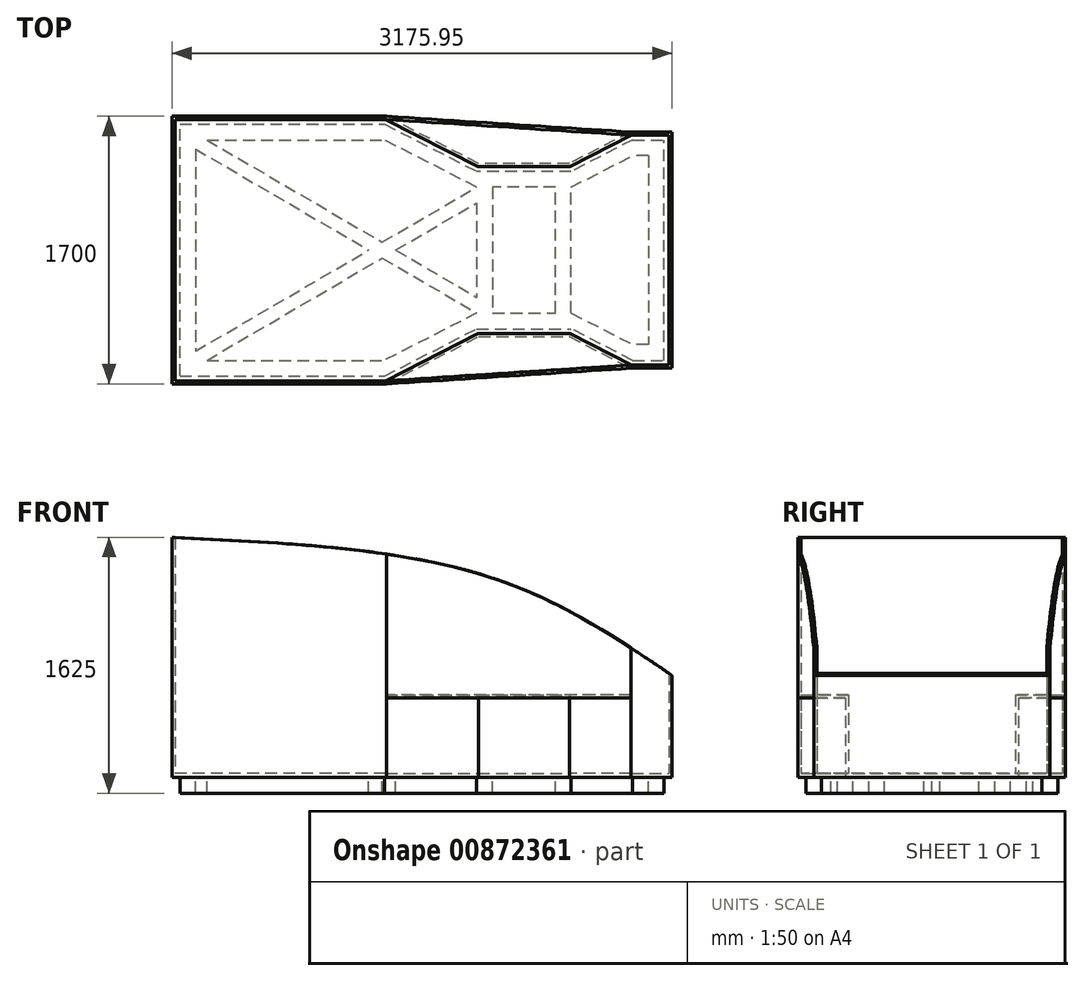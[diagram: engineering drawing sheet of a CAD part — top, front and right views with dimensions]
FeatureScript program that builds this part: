
annotation { "Feature Type Name" : "Feature", "Feature Type Description" : "" }
export const myFeature = defineFeature(function(context is Context, id is Id, definition is map)
    precondition{}
    {
        {
            var Q0;
            Q0=qCreatedBy(makeId("Top.planeOp"),FACE);
            var sketch = newSketch(context, id + "F0", { "sketchPlane" : qUnion([Q0])});
            skLineSegment(sketch, "E0", {"start": v(2008.61, 739.14) * mm, "end": v(1908.61, 739.14) * mm});
            skLineSegment(sketch, "E1.MirrorCS", {"start": v(-476.96, 1439.14) * mm, "end": v(-476.96, 1539.14) * mm});
            skLineSegment(sketch, "E2.MirrorCS", {"start": v(1408.61, 1039.14) * mm, "end": v(1408.61, 739.14) * mm});
            skLineSegment(sketch, "E3.MirrorCS", {"start": v(-476.96, 1539.14) * mm, "end": v(823.04, 1539.14) * mm});
            skLineSegment(sketch, "E4.MirrorCS", {"start": v(823.04, 1539.14) * mm, "end": v(1408.61, 1239.14) * mm});
            skLineSegment(sketch, "E5.MirrorCS", {"start": v(1408.61, 1139.14) * mm, "end": v(823.04, 1439.14) * mm});
            skLineSegment(sketch, "E6.MirrorCS", {"start": v(-305.54, 1439.14) * mm, "end": v(823.04, 1439.14) * mm});
            skLineSegment(sketch, "E7.MirrorCS", {"start": v(1408.61, 1239.14) * mm, "end": v(1708.61, 1239.14) * mm});
            skLineSegment(sketch, "E8.MirrorCS", {"start": v(1508.61, 739.14) * mm, "end": v(1508.61, 1139.14) * mm});
            skLineSegment(sketch, "E9.MirrorCS", {"start": v(1708.61, 1139.14) * mm, "end": v(1508.61, 1139.14) * mm});
            skLineSegment(sketch, "E10.MirrorCS", {"start": v(1708.61, 1139.14) * mm, "end": v(1908.61, 1139.14) * mm});
            skLineSegment(sketch, "E11.MirrorCS", {"start": v(1908.61, 739.14) * mm, "end": v(1908.61, 1139.14) * mm});
            skLineSegment(sketch, "E12.MirrorCS", {"start": v(2399, 1439.14) * mm, "end": v(2008.61, 1239.14) * mm});
            skLineSegment(sketch, "E13.MirrorCS", {"start": v(2008.61, 1139.14) * mm, "end": v(2399, 1339.14) * mm});
            skLineSegment(sketch, "E14.MirrorCS", {"start": v(2008.61, 1239.14) * mm, "end": v(1708.61, 1239.14) * mm});
            skLineSegment(sketch, "E15.MirrorCS", {"start": v(2008.61, 1139.14) * mm, "end": v(2008.61, 739.14) * mm});
            skLineSegment(sketch, "E16", {"start": v(2399, 1439.14) * mm, "end": v(2599, 1439.14) * mm});
            skLineSegment(sketch, "E17", {"start": v(2599, 1439.14) * mm, "end": v(2599, 1339.14) * mm});
            skLineSegment(sketch, "E18", {"start": v(2499, 1339.14) * mm, "end": v(2399, 1339.14) * mm});
            skLineSegment(sketch, "E19", {"start": v(2599, 739.14) * mm, "end": v(2599, 1339.14) * mm});
            skLineSegment(sketch, "E20", {"start": v(2499, 1339.14) * mm, "end": v(2499, 739.14) * mm});
            skLineSegment(sketch, "E21.MirrorCS", {"start": v(2599, 39.14) * mm, "end": v(2599, 139.14) * mm});
            skLineSegment(sketch, "E22.MirrorCS", {"start": v(-476.96, 39.14) * mm, "end": v(-476.96, -60.86) * mm});
            skLineSegment(sketch, "E23.MirrorCS", {"start": v(2499, 139.14) * mm, "end": v(2399, 139.14) * mm});
            skLineSegment(sketch, "E24.MirrorCS", {"start": v(2399, 39.14) * mm, "end": v(2599, 39.14) * mm});
            skLineSegment(sketch, "E25.MirrorCS", {"start": v(1408.61, 239.14) * mm, "end": v(1708.61, 239.14) * mm});
            skLineSegment(sketch, "E26.MirrorCS", {"start": v(-305.54, 39.14) * mm, "end": v(823.04, 39.14) * mm});
            skLineSegment(sketch, "E27.MirrorCS", {"start": v(-476.96, -60.86) * mm, "end": v(823.04, -60.86) * mm});
            skLineSegment(sketch, "E28.MirrorCS", {"start": v(823.04, -60.86) * mm, "end": v(1408.61, 239.14) * mm});
            skLineSegment(sketch, "E29.MirrorCS", {"start": v(1708.61, 339.14) * mm, "end": v(1908.61, 339.14) * mm});
            skLineSegment(sketch, "E30.MirrorCS", {"start": v(1408.61, 339.14) * mm, "end": v(823.04, 39.14) * mm});
            skLineSegment(sketch, "E31.MirrorCS", {"start": v(2008.61, 339.14) * mm, "end": v(2399, 139.14) * mm});
            skLineSegment(sketch, "E32.MirrorCS", {"start": v(1408.61, 439.14) * mm, "end": v(1408.61, 739.14) * mm});
            skLineSegment(sketch, "E33.MirrorCS", {"start": v(1708.61, 339.14) * mm, "end": v(1508.61, 339.14) * mm});
            skLineSegment(sketch, "E34.MirrorCS", {"start": v(2399, 39.14) * mm, "end": v(2008.61, 239.14) * mm});
            skLineSegment(sketch, "E35.MirrorCS", {"start": v(1508.61, 739.14) * mm, "end": v(1508.61, 339.14) * mm});
            skLineSegment(sketch, "E36.MirrorCS", {"start": v(1908.61, 739.14) * mm, "end": v(1908.61, 339.14) * mm});
            skLineSegment(sketch, "E37.MirrorCS", {"start": v(2599, 739.14) * mm, "end": v(2599, 139.14) * mm});
            skLineSegment(sketch, "E38.MirrorCS", {"start": v(2499, 139.14) * mm, "end": v(2499, 739.14) * mm});
            skLineSegment(sketch, "E39.MirrorCS", {"start": v(2008.61, 339.14) * mm, "end": v(2008.61, 739.14) * mm});
            skLineSegment(sketch, "E40.MirrorCS", {"start": v(2008.61, 239.14) * mm, "end": v(1708.61, 239.14) * mm});
            skPoint(sketch, "E41.MirrorCS.end.orphan", {"position": v(1018.23, 39.14) * mm});
            skPoint(sketch, "E42.end.orphan", {"position": v(1018.23, 1439.14) * mm});
            skLineSegment(sketch, "E43", {"start": v(-376.96, 1380.8) * mm, "end": v(722.95, 739.14) * mm});
            skLineSegment(sketch, "E44", {"start": v(-376.96, 97.48) * mm, "end": v(722.95, 739.14) * mm});
            skPoint(sketch, "E45", {"position": v(-305.54, 39.14) * mm});
            skPoint(sketch, "E46", {"position": v(1408.61, 1039.14) * mm});
            skLineSegment(sketch, "E47", {"start": v(-305.54, 39.14) * mm, "end": v(808.66, 689.14) * mm});
            skLineSegment(sketch, "E48", {"start": v(-305.54, 1439.14) * mm, "end": v(808.66, 789.14) * mm});
            skLineSegment(sketch, "E49.trimOffspring", {"start": v(808.66, 689.14) * mm, "end": v(1408.61, 339.14) * mm});
            skLineSegment(sketch, "E50.trimOffspring", {"start": v(808.66, 789.14) * mm, "end": v(1408.61, 1139.14) * mm});
            skLineSegment(sketch, "E51.trimOffspring", {"start": v(894.37, 739.14) * mm, "end": v(1408.61, 439.14) * mm});
            skLineSegment(sketch, "E52.trimOffspring", {"start": v(894.37, 739.14) * mm, "end": v(1408.61, 1039.14) * mm});
            skLineSegment(sketch, "E53", {"start": v(-476.96, 39.14) * mm, "end": v(-476.96, 1439.14) * mm});
            skLineSegment(sketch, "E54", {"start": v(-376.96, 1380.8) * mm, "end": v(-376.96, 97.48) * mm});
            skPoint(sketch, "E55", {"position": v(1608.61, 289.14) * mm});
            skPoint(sketch, "E56", {"position": v(1808.61, 289.14) * mm});
            skPoint(sketch, "E57", {"position": v(1608.61, 1189.14) * mm});
            skPoint(sketch, "E58", {"position": v(1808.61, 1189.14) * mm});
            skPoint(sketch, "E59.MirrorCS.end.orphan", {"position": v(1508.61, 739.14) * mm});
            skPoint(sketch, "E59.MirrorCS.start.orphan", {"position": v(1408.61, 739.14) * mm});
            skPoint(sketch, "E60.MirrorCS.end.orphan", {"position": v(1908.61, 739.14) * mm});
            skPoint(sketch, "E60.MirrorCS.start.orphan", {"position": v(2008.61, 739.14) * mm});
            skSolve(sketch);
        }
        {
            var Q0;
            Q0=makeQuery(id+"F0.imprint","IMPRINT",FACE,{"disambiguationData":[TD([[makeQuery(id+"F0.imprint","IMPRINT",EDGE,{"derivedFrom":sQuery(id+"F0.wireOp",EDGE,"E1.MirrorCS")}),-1.0]])]});
            extrude(context, id + "F1", {"entities" : qUnion([Q0]), "depth" : -100 * mm, "offsetDistance" : 25 * mm});
        }
        {
            var Q0;
            Q0=makeQuery(id+"F0.imprint","IMPRINT",FACE,{"disambiguationData":[TD([[makeQuery(id+"F0.imprint","IMPRINT",EDGE,{"derivedFrom":sQuery(id+"F0.wireOp",EDGE,"E1.MirrorCS")}),-1.0]])]});
            var sketch = newSketch(context, id + "F2", { "sketchPlane" : qUnion([Q0])});
            skLineSegment(sketch, "E61.0", {"start": v(1420.68, 189.14) * mm, "end": v(1708.61, 189.14) * mm});
            skLineSegment(sketch, "E61.1", {"start": v(835.1, -110.86) * mm, "end": v(1420.68, 189.14) * mm});
            skLineSegment(sketch, "E61.2", {"start": v(-526.96, -110.86) * mm, "end": v(835.1, -110.86) * mm});
            skLineSegment(sketch, "E61.3", {"start": v(-526.96, 39.14) * mm, "end": v(-526.96, -110.86) * mm});
            skLineSegment(sketch, "E61.4", {"start": v(-526.96, 1439.14) * mm, "end": v(-526.96, 39.14) * mm});
            skLineSegment(sketch, "E61.5", {"start": v(1708.61, 189.14) * mm, "end": v(1996.55, 189.14) * mm});
            skLineSegment(sketch, "E61.6", {"start": v(-526.96, 1589.14) * mm, "end": v(-526.96, 1439.14) * mm});
            skLineSegment(sketch, "E61.7", {"start": v(835.1, 1589.14) * mm, "end": v(-526.96, 1589.14) * mm});
            skLineSegment(sketch, "E61.8", {"start": v(1420.68, 1289.14) * mm, "end": v(835.1, 1589.14) * mm});
            skLineSegment(sketch, "E61.9", {"start": v(2649, 139.14) * mm, "end": v(2649, 739.14) * mm});
            skLineSegment(sketch, "E61.10", {"start": v(2649, -10.86) * mm, "end": v(2649, 139.14) * mm});
            skLineSegment(sketch, "E61.11", {"start": v(2386.93, -10.86) * mm, "end": v(2649, -10.86) * mm});
            skLineSegment(sketch, "E61.12", {"start": v(1996.55, 189.14) * mm, "end": v(2386.93, -10.86) * mm});
            skLineSegment(sketch, "E61.13", {"start": v(2649, 739.14) * mm, "end": v(2649, 1339.14) * mm});
            skLineSegment(sketch, "E61.14", {"start": v(2649, 1339.14) * mm, "end": v(2649, 1489.14) * mm});
            skLineSegment(sketch, "E61.15", {"start": v(2649, 1489.14) * mm, "end": v(2386.93, 1489.14) * mm});
            skLineSegment(sketch, "E61.16", {"start": v(2386.93, 1489.14) * mm, "end": v(1996.55, 1289.14) * mm});
            skLineSegment(sketch, "E61.17", {"start": v(1996.55, 1289.14) * mm, "end": v(1708.61, 1289.14) * mm});
            skLineSegment(sketch, "E61.18", {"start": v(1708.61, 1289.14) * mm, "end": v(1420.68, 1289.14) * mm});
            skSolve(sketch);
        }
        {
            var Q0;
            Q0=makeQuery(id+"F2.imprint","IMPRINT",FACE,{"disambiguationData":[TD([[makeQuery(id+"F2.imprint","IMPRINT",EDGE,{"derivedFrom":sQuery(id+"F2.wireOp",EDGE,"E61.0")}),1.0]])]});
            var Q1;
            Q1=makeQuery(id+"F2.imprint","IMPRINT",FACE,{"disambiguationData":[TD([[makeQuery(id+"F2.imprint","IMPRINT",EDGE,{"derivedFrom":makeQuery(id+"F0.imprint","IMPRINT",EDGE,{"derivedFrom":sQuery(id+"F0.wireOp",EDGE,"E1.MirrorCS")})}),-1.0]])]});
            var Q2;
            Q2=makeQuery(id+"F2.imprint","IMPRINT",FACE,{"disambiguationData":[TD([[makeQuery(id+"F2.imprint","IMPRINT",EDGE,{"derivedFrom":makeQuery(id+"F0.imprint","IMPRINT",EDGE,{"derivedFrom":sQuery(id+"F0.wireOp",EDGE,"E8.MirrorCS")})}),-1.0]])]});
            var Q3;
            Q3=makeQuery(id+"F2.imprint","IMPRINT",FACE,{"disambiguationData":[TD([[makeQuery(id+"F2.imprint","IMPRINT",EDGE,{"derivedFrom":makeQuery(id+"F0.imprint","IMPRINT",EDGE,{"derivedFrom":sQuery(id+"F0.wireOp",EDGE,"E2.MirrorCS")})}),-1.0]])]});
            var Q4;
            Q4=makeQuery(id+"F2.imprint","IMPRINT",FACE,{"disambiguationData":[TD([[makeQuery(id+"F2.imprint","IMPRINT",EDGE,{"derivedFrom":makeQuery(id+"F0.imprint","IMPRINT",EDGE,{"derivedFrom":sQuery(id+"F0.wireOp",EDGE,"E26.MirrorCS")})}),1.0]])]});
            var Q5;
            Q5=makeQuery(id+"F2.imprint","IMPRINT",FACE,{"disambiguationData":[TD([[makeQuery(id+"F2.imprint","IMPRINT",EDGE,{"derivedFrom":makeQuery(id+"F0.imprint","IMPRINT",EDGE,{"derivedFrom":sQuery(id+"F0.wireOp",EDGE,"E5.MirrorCS")})}),1.0]])]});
            var Q6;
            Q6=makeQuery(id+"F2.imprint","IMPRINT",FACE,{"disambiguationData":[TD([[makeQuery(id+"F2.imprint","IMPRINT",EDGE,{"derivedFrom":makeQuery(id+"F0.imprint","IMPRINT",EDGE,{"derivedFrom":sQuery(id+"F0.wireOp",EDGE,"E43")})}),-1.0]])]});
            var Q7;
            Q7=makeQuery(id+"F2.imprint","IMPRINT",FACE,{"disambiguationData":[TD([[makeQuery(id+"F2.imprint","IMPRINT",EDGE,{"derivedFrom":makeQuery(id+"F0.imprint","IMPRINT",EDGE,{"derivedFrom":sQuery(id+"F0.wireOp",EDGE,"E13.MirrorCS")})}),-1.0]])]});
            extrude(context, id + "F3", {"entities" : qUnion([Q0, Q1, Q2, Q3, Q4, Q5, Q6, Q7]), "operationType" : NewBodyOperationType.ADD, "depth" : 25 * mm, "offsetDistance" : 25 * mm});
        }
        {
            var Q0;
            Q0=makeQuery(id+"F3.opExtrude","CAP_FACE",FACE,{"disambiguationData":[OSD([sQuery(id+"F2.wireOp",EDGE,"E61.0"),sQuery(id+"F2.wireOp",EDGE,"E61.1"),sQuery(id+"F2.wireOp",EDGE,"E61.2"),sQuery(id+"F2.wireOp",EDGE,"E61.3"),sQuery(id+"F2.wireOp",EDGE,"E61.4"),sQuery(id+"F2.wireOp",EDGE,"E61.5"),sQuery(id+"F2.wireOp",EDGE,"E61.6"),sQuery(id+"F2.wireOp",EDGE,"E61.7"),sQuery(id+"F2.wireOp",EDGE,"E61.8"),sQuery(id+"F2.wireOp",EDGE,"E61.9"),sQuery(id+"F2.wireOp",EDGE,"E61.10"),sQuery(id+"F2.wireOp",EDGE,"E61.11"),sQuery(id+"F2.wireOp",EDGE,"E61.12"),sQuery(id+"F2.wireOp",EDGE,"E61.13"),sQuery(id+"F2.wireOp",EDGE,"E61.14"),sQuery(id+"F2.wireOp",EDGE,"E61.15"),sQuery(id+"F2.wireOp",EDGE,"E61.16"),sQuery(id+"F2.wireOp",EDGE,"E61.17"),sQuery(id+"F2.wireOp",EDGE,"E61.18")])],"isStart":false});
            var sketch = newSketch(context, id + "F4", { "sketchPlane" : qUnion([Q0])});
            skLineSegment(sketch, "E62.0", {"start": v(2391.76, 9.14) * mm, "end": v(2629, 9.14) * mm});
            skLineSegment(sketch, "E62.1", {"start": v(1415.85, 1269.14) * mm, "end": v(830.28, 1569.14) * mm});
            skLineSegment(sketch, "E62.2", {"start": v(2001.38, 1269.14) * mm, "end": v(1415.85, 1269.14) * mm});
            skLineSegment(sketch, "E62.3", {"start": v(2391.76, 1469.14) * mm, "end": v(2001.38, 1269.14) * mm});
            skLineSegment(sketch, "E62.4", {"start": v(2629, 1469.14) * mm, "end": v(2391.76, 1469.14) * mm});
            skLineSegment(sketch, "E62.5", {"start": v(830.28, 1569.14) * mm, "end": v(-506.96, 1569.14) * mm});
            skLineSegment(sketch, "E62.6", {"start": v(2629, 9.14) * mm, "end": v(2629, 1469.14) * mm});
            skLineSegment(sketch, "E62.7", {"start": v(-506.96, 1569.14) * mm, "end": v(-506.96, -90.86) * mm});
            skLineSegment(sketch, "E62.8", {"start": v(-506.96, -90.86) * mm, "end": v(830.28, -90.86) * mm});
            skLineSegment(sketch, "E62.9", {"start": v(830.28, -90.86) * mm, "end": v(1415.85, 209.14) * mm});
            skLineSegment(sketch, "E62.10", {"start": v(1415.85, 209.14) * mm, "end": v(2001.38, 209.14) * mm});
            skLineSegment(sketch, "E62.11", {"start": v(2001.38, 209.14) * mm, "end": v(2391.76, 9.14) * mm});
            skSolve(sketch);
        }
        {
            var Q0;
            Q0=makeQuery(id+"F4.imprint","IMPRINT",FACE,{"disambiguationData":[TD([[makeQuery(id+"F4.imprint","IMPRINT",EDGE,{"derivedFrom":sQuery(id+"F4.wireOp",EDGE,"E62.0")}),-1.0]])]});
            extrude(context, id + "F5", {"entities" : qUnion([Q0]), "operationType" : NewBodyOperationType.ADD, "depth" : 500 * mm, "offsetDistance" : 25 * mm});
        }
        {
            var Q0;
            Q0=makeQuery(id+"F5.opExtrude","CAP_FACE",FACE,{"disambiguationData":[OSD([sQuery(id+"F2.wireOp",EDGE,"E61.0"),sQuery(id+"F2.wireOp",EDGE,"E61.1"),sQuery(id+"F2.wireOp",EDGE,"E61.2"),sQuery(id+"F2.wireOp",EDGE,"E61.3"),sQuery(id+"F2.wireOp",EDGE,"E61.4"),sQuery(id+"F2.wireOp",EDGE,"E61.5"),sQuery(id+"F2.wireOp",EDGE,"E61.6"),sQuery(id+"F2.wireOp",EDGE,"E61.7"),sQuery(id+"F2.wireOp",EDGE,"E61.8"),sQuery(id+"F2.wireOp",EDGE,"E61.9"),sQuery(id+"F2.wireOp",EDGE,"E61.10"),sQuery(id+"F2.wireOp",EDGE,"E61.11"),sQuery(id+"F2.wireOp",EDGE,"E61.12"),sQuery(id+"F2.wireOp",EDGE,"E61.13"),sQuery(id+"F2.wireOp",EDGE,"E61.14"),sQuery(id+"F2.wireOp",EDGE,"E61.15"),sQuery(id+"F2.wireOp",EDGE,"E61.16"),sQuery(id+"F2.wireOp",EDGE,"E61.17"),sQuery(id+"F2.wireOp",EDGE,"E61.18"),sQuery(id+"F4.wireOp",EDGE,"E62.0"),sQuery(id+"F4.wireOp",EDGE,"E62.1"),sQuery(id+"F4.wireOp",EDGE,"E62.2"),sQuery(id+"F4.wireOp",EDGE,"E62.3"),sQuery(id+"F4.wireOp",EDGE,"E62.4"),sQuery(id+"F4.wireOp",EDGE,"E62.5"),sQuery(id+"F4.wireOp",EDGE,"E62.6"),sQuery(id+"F4.wireOp",EDGE,"E62.7"),sQuery(id+"F4.wireOp",EDGE,"E62.8"),sQuery(id+"F4.wireOp",EDGE,"E62.9"),sQuery(id+"F4.wireOp",EDGE,"E62.10"),sQuery(id+"F4.wireOp",EDGE,"E62.11")])],"isStart":false});
            var sketch = newSketch(context, id + "F6", { "sketchPlane" : qUnion([Q0])});
            skLineSegment(sketch, "E63", {"start": v(835.1, -110.86) * mm, "end": v(2386.93, -10.86) * mm});
            skLineSegment(sketch, "E64", {"start": v(835.1, 1589.14) * mm, "end": v(2386.93, 1489.14) * mm});
            skSolve(sketch);
        }
        {
            var Q0;
            Q0=makeQuery(id+"F6.imprint","IMPRINT",FACE,{"disambiguationData":[TD([[makeQuery(id+"F6.imprint","IMPRINT",EDGE,{"derivedFrom":sQuery(id+"F6.wireOp",EDGE,"E63")}),1.0]])]});
            var Q1;
            Q1=makeQuery(id+"F6.imprint","IMPRINT",FACE,{"disambiguationData":[TD([[makeQuery(id+"F6.imprint","IMPRINT",EDGE,{"derivedFrom":sQuery(id+"F6.wireOp",EDGE,"E64")}),-1.0]])]});
            extrude(context, id + "F7", {"entities" : qUnion([Q0, Q1]), "operationType" : NewBodyOperationType.ADD, "depth" : -20 * mm, "offsetDistance" : 25 * mm});
        }
        {
            var Q0;
            {var subQ0=sQuery(id+"F2.wireOp",EDGE,"E61.18");var subQ1=sQuery(id+"F2.wireOp",EDGE,"E61.17");var subQ2=sQuery(id+"F2.wireOp",EDGE,"E61.16");var subQ3=sQuery(id+"F2.wireOp",EDGE,"E61.8");var subQ4=sQuery(id+"F2.wireOp",EDGE,"E61.12");var subQ5=sQuery(id+"F2.wireOp",EDGE,"E61.5");var subQ6=sQuery(id+"F2.wireOp",EDGE,"E61.1");var subQ7=sQuery(id+"F2.wireOp",EDGE,"E61.0");Q0=makeQuery(id+"F7.boolean.opBoolean","MERGE",FACE,{"derivedFrom":[makeQuery(id+"F5.opExtrude","CAP_FACE",FACE,{"disambiguationData":[OSD([subQ7,subQ6,sQuery(id+"F2.wireOp",EDGE,"E61.2"),sQuery(id+"F2.wireOp",EDGE,"E61.3"),sQuery(id+"F2.wireOp",EDGE,"E61.4"),subQ5,sQuery(id+"F2.wireOp",EDGE,"E61.6"),sQuery(id+"F2.wireOp",EDGE,"E61.7"),subQ3,sQuery(id+"F2.wireOp",EDGE,"E61.9"),sQuery(id+"F2.wireOp",EDGE,"E61.10"),sQuery(id+"F2.wireOp",EDGE,"E61.11"),subQ4,sQuery(id+"F2.wireOp",EDGE,"E61.13"),sQuery(id+"F2.wireOp",EDGE,"E61.14"),sQuery(id+"F2.wireOp",EDGE,"E61.15"),subQ2,subQ1,subQ0,sQuery(id+"F4.wireOp",EDGE,"E62.0"),sQuery(id+"F4.wireOp",EDGE,"E62.1"),sQuery(id+"F4.wireOp",EDGE,"E62.2"),sQuery(id+"F4.wireOp",EDGE,"E62.3"),sQuery(id+"F4.wireOp",EDGE,"E62.4"),sQuery(id+"F4.wireOp",EDGE,"E62.5"),sQuery(id+"F4.wireOp",EDGE,"E62.6"),sQuery(id+"F4.wireOp",EDGE,"E62.7"),sQuery(id+"F4.wireOp",EDGE,"E62.8"),sQuery(id+"F4.wireOp",EDGE,"E62.9"),sQuery(id+"F4.wireOp",EDGE,"E62.10"),sQuery(id+"F4.wireOp",EDGE,"E62.11")])],"isStart":false}),makeQuery(id+"F7.opExtrude","CAP_FACE",FACE,{"disambiguationData":[OSD([subQ7,subQ6,subQ5,subQ4,sQuery(id+"F6.wireOp",EDGE,"E63")])],"isStart":true}),makeQuery(id+"F7.opExtrude","CAP_FACE",FACE,{"disambiguationData":[OSD([subQ3,subQ2,subQ1,subQ0,sQuery(id+"F6.wireOp",EDGE,"E64")])],"isStart":true})]});}
            var sketch = newSketch(context, id + "F8", { "sketchPlane" : qUnion([Q0])});
            skLineSegment(sketch, "E65.0", {"start": v(2629, 1469.14) * mm, "end": v(2386.29, 1469.14) * mm});
            skLineSegment(sketch, "E65.1", {"start": v(2629, 9.14) * mm, "end": v(2629, 1469.14) * mm});
            skLineSegment(sketch, "E65.2", {"start": v(2386.29, 1469.14) * mm, "end": v(834.46, 1569.14) * mm});
            skLineSegment(sketch, "E65.3", {"start": v(2386.29, 9.14) * mm, "end": v(2629, 9.14) * mm});
            skLineSegment(sketch, "E65.4", {"start": v(834.46, 1569.14) * mm, "end": v(-506.96, 1569.14) * mm});
            skLineSegment(sketch, "E65.5", {"start": v(-506.96, 1569.14) * mm, "end": v(-506.96, -90.86) * mm});
            skLineSegment(sketch, "E65.6", {"start": v(-506.96, -90.86) * mm, "end": v(834.46, -90.86) * mm});
            skLineSegment(sketch, "E65.7", {"start": v(834.46, -90.86) * mm, "end": v(2386.29, 9.14) * mm});
            skSolve(sketch);
        }
        {
            var Q0;
            {var subQ8=sQuery(id+"F8.wireOp",EDGE,"E65.1");Q0=makeQuery(id+"F8.imprint","IMPRINT",FACE,{"disambiguationData":[TD([[makeQuery(id+"F8.imprint","IMPRINT",EDGE,{"derivedFrom":subQ8}),-1.0]])]});}
            extrude(context, id + "F9", {"entities" : qUnion([Q0]), "operationType" : NewBodyOperationType.ADD, "depth" : 1000 * mm, "offsetDistance" : 25 * mm});
        }
        {
            var Q0;
            {var subQ0=sQuery(id+"F2.wireOp",EDGE,"E61.2");Q0=makeQuery(id+"F9.boolean.opBoolean","MERGE",FACE,{"derivedFrom":[makeQuery(id+"F5.boolean.opBoolean","MERGE",FACE,{"derivedFrom":[makeQuery(id+"F3.opExtrude","SWEPT_FACE",FACE,{"disambiguationData":[OSD([subQ0])]}),makeQuery(id+"F5.opExtrude","SWEPT_FACE",FACE,{"disambiguationData":[OSD([subQ0])]})]}),makeQuery(id+"F9.opExtrude","SWEPT_FACE",FACE,{"disambiguationData":[OSD([subQ0])]})]});}
            var sketch = newSketch(context, id + "F10", { "sketchPlane" : qUnion([Q0])});
            skFitSpline(sketch, "E66", {"points": [v(-526.96, 1525) * mm, v(1472.77, 1278.73) * mm, v(2649, 648.63) * mm], "startDerivative": vector(3904.66, -183.1) * mm, "endDerivative": vector(2400.37, -1618.57) * mm});
            skLineSegment(sketch, "E67", {"start": v(-526.96, 1525) * mm, "end": v(2649, 1525) * mm});
            skLineSegment(sketch, "E68", {"start": v(2649, 1525) * mm, "end": v(2649, 648.63) * mm});
            skSolve(sketch);
        }
        {
            var Q0;
            {var subQ1=sQuery(id+"F10.wireOp",EDGE,"E66");var subQ5=sQuery(id+"F2.wireOp",EDGE,"E61.2");var subQ7=sQuery(id+"F6.wireOp",EDGE,"E63");var subQ8=sQuery(id+"F2.wireOp",EDGE,"E61.1");var subQ9=makeQuery(id+"F9.boolean.opBoolean","MERGE",EDGE,{"derivedFrom":[makeQuery(id+"F7.boolean.opBoolean","MERGE",EDGE,{"derivedFrom":[makeQuery(id+"F5.boolean.opBoolean","MERGE",EDGE,{"derivedFrom":[makeQuery(id+"F3.opExtrude","SWEPT_EDGE",EDGE,{"disambiguationData":[OSD([subQ8,subQ5])]}),makeQuery(id+"F5.opExtrude","SWEPT_EDGE",EDGE,{"disambiguationData":[OSD([subQ8,subQ5])]})]}),makeQuery(id+"F7.opExtrude","SWEPT_EDGE",EDGE,{"disambiguationData":[OSD([subQ8,subQ5,subQ7])]})]}),makeQuery(id+"F9.opExtrude","SWEPT_EDGE",EDGE,{"disambiguationData":[OSD([subQ5,subQ7])]})]});var subQ10=makeQuery(id+"F10.imprint","INTERSECT",VERTEX,{"derivedFrom":[subQ9,subQ1]});Q0=makeQuery(id+"F10.imprint","IMPRINT",FACE,{"disambiguationData":[TD([[makeQuery(id+"F10.imprint","IMPRINT",EDGE,{"disambiguationData":[TD([[subQ10,1.0]])],"derivedFrom":subQ1}),1.0]])]});}
            var Q1;
            {var subQ0=sQuery(id+"F10.wireOp",EDGE,"E68");Q1=makeQuery(id+"F10.imprint","IMPRINT",FACE,{"disambiguationData":[TD([[makeQuery(id+"F10.imprint","IMPRINT",EDGE,{"derivedFrom":subQ0}),-1.0]])]});}
            extrude(context, id + "F11", {"entities" : qUnion([Q0, Q1]), "operationType" : NewBodyOperationType.REMOVE, "depth" : -2000 * mm, "offsetDistance" : 25 * mm});
        }
    });
